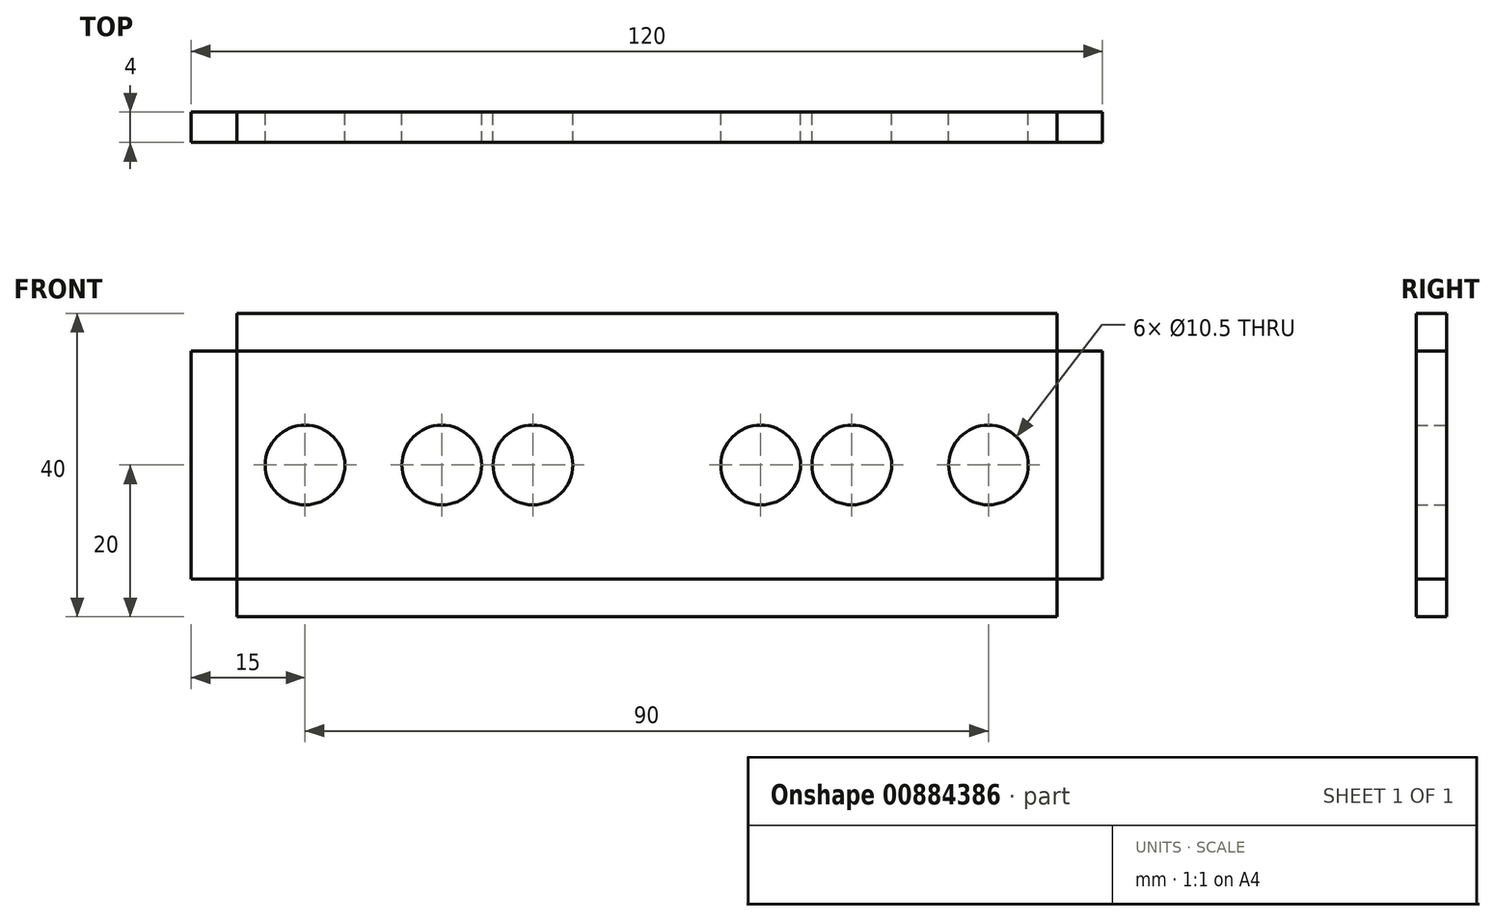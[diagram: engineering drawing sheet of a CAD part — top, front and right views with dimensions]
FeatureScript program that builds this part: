
annotation { "Feature Type Name" : "Feature", "Feature Type Description" : "" }
export const myFeature = defineFeature(function(context is Context, id is Id, definition is map)
    precondition{}
    {
        {
            var Q0;
            Q0=qCreatedBy(makeId("Front.planeOp"),FACE);
            var sketch = newSketch(context, id + "F0", { "sketchPlane" : qUnion([Q0])});
            skLineSegment(sketch, "E0.bottom", {"start": v(60, 15) * mm, "end": v(-60, 15) * mm});
            skLineSegment(sketch, "E0.top", {"start": v(60, -15) * mm, "end": v(-60, -15) * mm});
            skLineSegment(sketch, "E0.left", {"start": v(60, 15) * mm, "end": v(60, -15) * mm});
            skLineSegment(sketch, "E0.right", {"start": v(-60, 15) * mm, "end": v(-60, -15) * mm});
            skPoint(sketch, "E0.middle", {"position": v(0, 0) * mm});
            skCircle(sketch, "E1", {"center": v(-45, 0) * mm, "radius": 5.25 * mm});
            skCircle(sketch, "E2", {"center": v(-15, 0) * mm, "radius": 5.25 * mm});
            skCircle(sketch, "E3", {"center": v(15, 0) * mm, "radius": 5.25 * mm});
            skCircle(sketch, "E4", {"center": v(45, 0) * mm, "radius": 5.25 * mm});
            skSolve(sketch);
        }
        {
            var Q0;
            Q0=makeQuery(id+"F0.imprint","IMPRINT",FACE,{"disambiguationData":[TD([[makeQuery(id+"F0.imprint","IMPRINT",EDGE,{"derivedFrom":sQuery(id+"F0.wireOp",EDGE,"E0.bottom")}),1.0]])]});
            extrude(context, id + "F1", {"entities" : qUnion([Q0]), "depth" : 4 * mm, "offsetDistance" : 25 * mm});
        }
        {
            var Q0;
            Q0=qCreatedBy(makeId("Front.planeOp"),FACE);
            var sketch = newSketch(context, id + "F2", { "sketchPlane" : qUnion([Q0])});
            skLineSegment(sketch, "E5.bottom", {"start": v(-54, 20) * mm, "end": v(54, 20) * mm});
            skLineSegment(sketch, "E5.top", {"start": v(-54, -20) * mm, "end": v(54, -20) * mm});
            skLineSegment(sketch, "E5.left", {"start": v(-54, 20) * mm, "end": v(-54, -20) * mm});
            skLineSegment(sketch, "E5.right", {"start": v(54, 20) * mm, "end": v(54, -20) * mm});
            skPoint(sketch, "E5.middle", {"position": v(0, 0) * mm});
            skCircle(sketch, "E6", {"center": v(-27, 0) * mm, "radius": 5.25 * mm});
            skCircle(sketch, "E7", {"center": v(27, 0) * mm, "radius": 5.25 * mm});
            skText(sketch, "E8", { "text": "16 stuks", "fontName": "OpenSans-Regular.ttf"});
            const initialGuessF2  = {"E8": [-0.03243, -0.04255, 1, 0, 0.0121]};
            skSetInitialGuess(sketch, initialGuessF2);
            skSolve(sketch);
        }
        {
            var Q0;
            Q0=makeQuery(id+"F2.imprint","IMPRINT",FACE,{"disambiguationData":[TD([[makeQuery(id+"F2.imprint","IMPRINT",EDGE,{"derivedFrom":sQuery(id+"F2.wireOp",EDGE,"E5.bottom")}),-1.0]])]});
            extrude(context, id + "F3", {"entities" : qUnion([Q0]), "depth" : 4 * mm, "offsetDistance" : 25 * mm});
        }
    });
